# Revit family: Faucet-Single-DXV-Modulus-D35120102_Series
name_source: partatom
category: Plumbing Fixtures
revit_build: Autodesk Revit 2014 (Build: 20130308_1515(x64)
units: mm (PartAtom-declared; Revit-internal decimal feet)

## types (4) — shared parameters
ADA Compliant = Yes
Assembly Code = D2020300
CW Connection = Yes
CWFU = 1.5
CalGreen Compliant = Yes
Cold Water Connection Radius = 3/16"
Cold Water Diameter = 3/8"
Default Elevation = 0"
Description = DXV Modulus Single Lever Lavatory Faucet
Flow Rate = 1.2 gpm (4.5 L/min)
HW Connection = Yes
HWFU = 1.5
Height = 5"
Hot Water Connection Diameter = 3/8"
Hot Water Connection Radius = 3/16"
Installation Type = Deck Mounted
Length = 6 15/16"
Manufacturer = DXV
Price = Prices may vary. Please consult Manufacturer Rep for most up-to-date price list.
Product Page URL = https://www.dxv.com
URL = https://www.dxv.com
Vent Connection = No
WFU = 2
Waste Connection = No
Width = 2 9/16"

## per-type parameters (varying)
| type | Finish | Material |
| D35120102.100 | Metal-DXV-100-Polished Chrome | Metal-DXV-100-Polished Chrome |
| D35120102.144 | Metal-DXV-144-Brushed Nickel | Metal-DXV-144-Brushed Nickel |
| D35120102.150 | Metal-DXV-150-Platinum Nickel | Metal-DXV-150-Platinum Nickel |
| D35120102.243 | Metal-DXV-243-Matte Black | Metal-DXV-243-Matte Black |

note: column(s) folded — value = type name in every type: Model

## geometry (parser evidence)
native form markers: Sweep x1
no freeform markers — native parametric forms only
